# Revit family: Bottle_Filler-Oasis-Aqua_Pointe_Sports_Bottle_Filler-MWG8SBF
name_source: partatom
category: Plumbing Fixtures
revit_build: Autodesk Revit MEP 2013 (Build: 20130531_2115(x64)
units: mm (PartAtom-declared; Revit-internal decimal feet)

## types (2) — shared parameters
CW Connection = No
Chiller = Yes
Cold Water Connector = Cold Water Connection
Cold Water Diameter = 0"
Cold Water Radius = 0"
Compression HP = 0 VA
Default Elevation = 4' - 0"
Description = Aqua Pointe Sports Bottle Filler
Finish = Metal - Oasis International - Brushed Stainless Steel - Exterior Finish
Full Load Amps = 5 A
Manufacturer = Oasis International
Manufacturer Fax Number = (614)322-4557
Metal Finish = Metal - Oasis International - Brushed Stainless Steel - Exterior Finish
Number of Poles = 1
Power Factor = 1
Product Documentation Link = http://www.oasiscoolers.com
Product Name = Sports Bottle Filler
Product Page URL = http://www.oasiscoolers.com
Sanitary Connector = Sanitary Connection
Sanitary Diameter = 0"
Sanitary Radius = 0"
URL = http://www.oasiscoolers.com
Voltage = 115 V
Waste Connection = No
Width = 3' - 2 3/4"
zero-valued in all types: CWFU, WFU

## per-type parameters (varying)
| type | Apparent Load | Base Rate | Rated Capacity | Rated Watts |
| MWG8SBF | 550 VA | 8 GPM | 8 GPM | 550 W |
| MWG12SBF | 620 VA | 12 GPM | 12 GPM | 620 W |

note: column(s) folded — value = type name in every type: Model

## geometry (parser evidence)
native form markers: Blend x12, Sweep x13
no freeform markers — native parametric forms only
